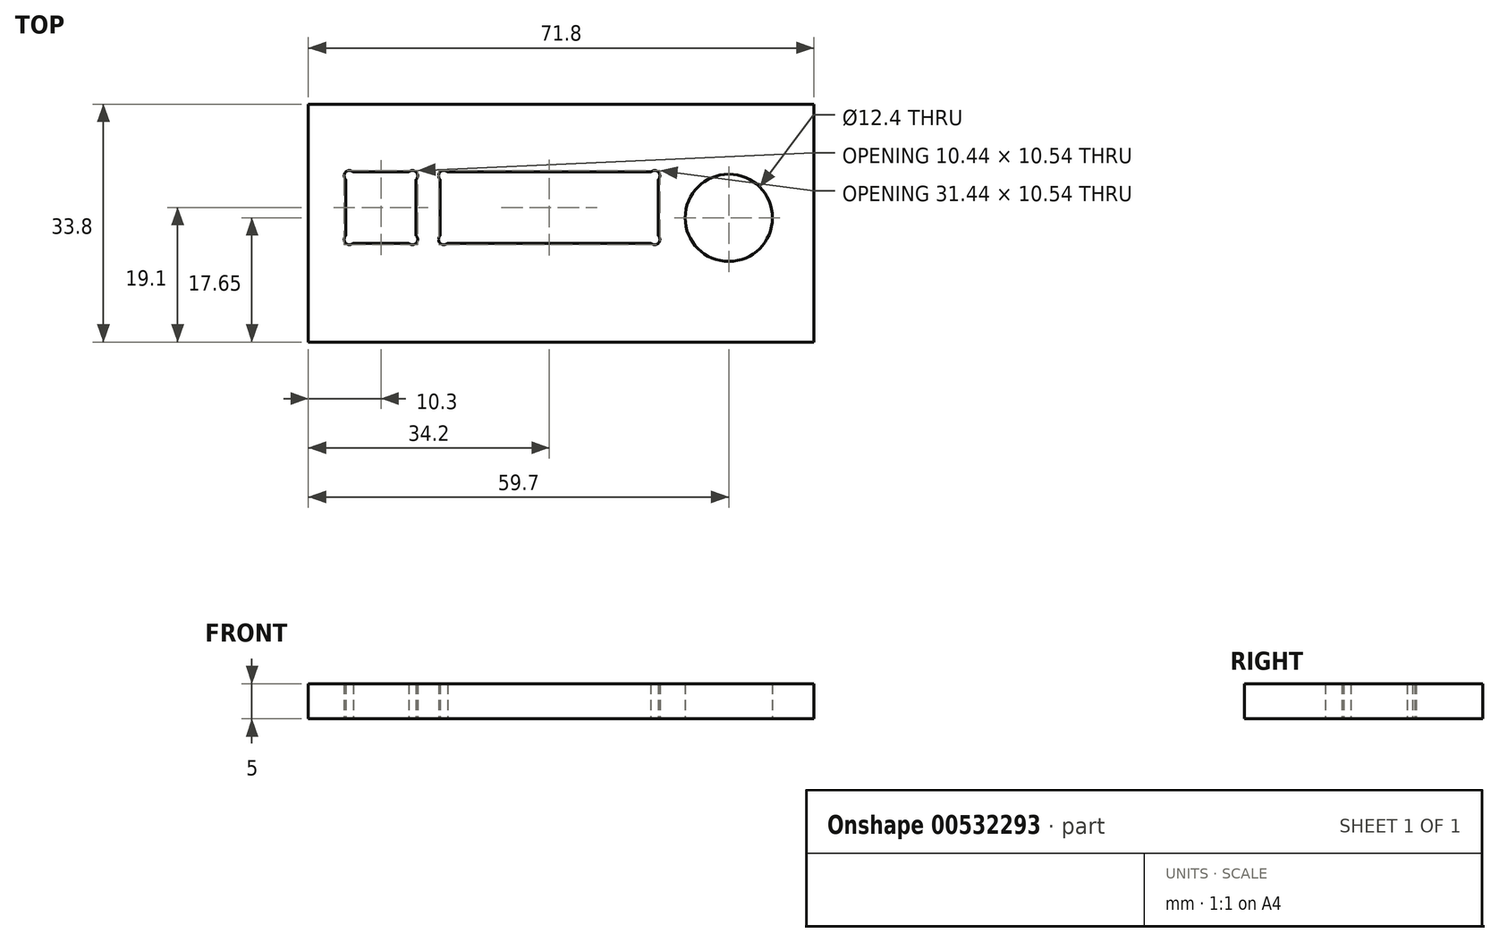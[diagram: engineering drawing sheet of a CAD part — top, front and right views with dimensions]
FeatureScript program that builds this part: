
annotation { "Feature Type Name" : "Feature", "Feature Type Description" : "" }
export const myFeature = defineFeature(function(context is Context, id is Id, definition is map)
    precondition{}
    {
        {
            var Q0;
            Q0=qCreatedBy(makeId("Top.planeOp"),FACE);
            var sketch = newSketch(context, id + "F0", { "sketchPlane" : qUnion([Q0])});
            skLineSegment(sketch, "E0.bottom", {"start": v(35.9, 16.9) * mm, "end": v(-35.9, 16.9) * mm});
            skLineSegment(sketch, "E0.top", {"start": v(35.9, -16.9) * mm, "end": v(-35.9, -16.9) * mm});
            skLineSegment(sketch, "E0.left", {"start": v(35.9, 16.9) * mm, "end": v(35.9, -16.9) * mm});
            skLineSegment(sketch, "E0.right", {"start": v(-35.9, 16.9) * mm, "end": v(-35.9, -16.9) * mm});
            skPoint(sketch, "E0.middle", {"position": v(0, 0) * mm});
            skLineSegment(sketch, "E1.bottom", {"start": v(-17.2, 7.25) * mm, "end": v(13.8, 7.25) * mm});
            skLineSegment(sketch, "E1.top", {"start": v(-17.2, -2.85) * mm, "end": v(13.8, -2.85) * mm});
            skLineSegment(sketch, "E1.left", {"start": v(-17.2, 7.25) * mm, "end": v(-17.2, -2.85) * mm});
            skLineSegment(sketch, "E1.right", {"start": v(13.8, 7.25) * mm, "end": v(13.8, -2.85) * mm});
            skLineSegment(sketch, "E2.bottom", {"start": v(-30.6, 7.25) * mm, "end": v(-20.6, 7.25) * mm});
            skLineSegment(sketch, "E2.top", {"start": v(-30.6, -2.85) * mm, "end": v(-20.6, -2.85) * mm});
            skLineSegment(sketch, "E2.left", {"start": v(-30.6, 7.25) * mm, "end": v(-30.6, -2.85) * mm});
            skLineSegment(sketch, "E2.right", {"start": v(-20.6, 7.25) * mm, "end": v(-20.6, -2.85) * mm});
            skCircle(sketch, "E3", {"center": v(23.8, 0.75) * mm, "radius": 6.2 * mm});
            skLineSegment(sketch, "E4", {"start": v(-30.6, 7.25) * mm, "end": v(-30.07, 6.72) * mm, "construction": true});
            skCircle(sketch, "E5", {"center": v(-30.07, 6.72) * mm, "radius": 0.75 * mm});
            skLineSegment(sketch, "E6", {"start": v(-20.6, 7.25) * mm, "end": v(-21.13, 6.72) * mm, "construction": true});
            skLineSegment(sketch, "E7", {"start": v(-20.6, -2.85) * mm, "end": v(-21.13, -2.32) * mm, "construction": true});
            skLineSegment(sketch, "E8", {"start": v(-30.6, -2.85) * mm, "end": v(-30.07, -2.32) * mm, "construction": true});
            skCircle(sketch, "E9", {"center": v(-30.07, -2.32) * mm, "radius": 0.75 * mm});
            skCircle(sketch, "E10", {"center": v(-21.13, -2.32) * mm, "radius": 0.75 * mm});
            skCircle(sketch, "E11", {"center": v(-21.13, 6.72) * mm, "radius": 0.75 * mm});
            skLineSegment(sketch, "E12", {"start": v(-17.2, 7.25) * mm, "end": v(-16.67, 6.72) * mm, "construction": true});
            skLineSegment(sketch, "E13", {"start": v(-17.2, -2.85) * mm, "end": v(-16.67, -2.32) * mm, "construction": true});
            skLineSegment(sketch, "E14", {"start": v(13.8, -2.85) * mm, "end": v(13.27, -2.32) * mm, "construction": true});
            skLineSegment(sketch, "E15", {"start": v(13.8, 7.25) * mm, "end": v(13.27, 6.72) * mm, "construction": true});
            skCircle(sketch, "E16", {"center": v(13.27, 6.72) * mm, "radius": 0.75 * mm});
            skCircle(sketch, "E17", {"center": v(13.27, -2.32) * mm, "radius": 0.75 * mm});
            skCircle(sketch, "E18", {"center": v(-16.67, -2.32) * mm, "radius": 0.75 * mm});
            skCircle(sketch, "E19", {"center": v(-16.67, 6.72) * mm, "radius": 0.75 * mm});
            skSolve(sketch);
        }
        {
            var Q0;
            Q0=makeQuery(id+"F0.imprint","IMPRINT",FACE,{"disambiguationData":[TD([[makeQuery(id+"F0.imprint","IMPRINT",EDGE,{"derivedFrom":sQuery(id+"F0.wireOp",EDGE,"E0.bottom")}),1.0]])]});
            extrude(context, id + "F1", {"entities" : qUnion([Q0]), "depth" : 5 * mm, "offsetDistance" : 25 * mm});
        }
    });
